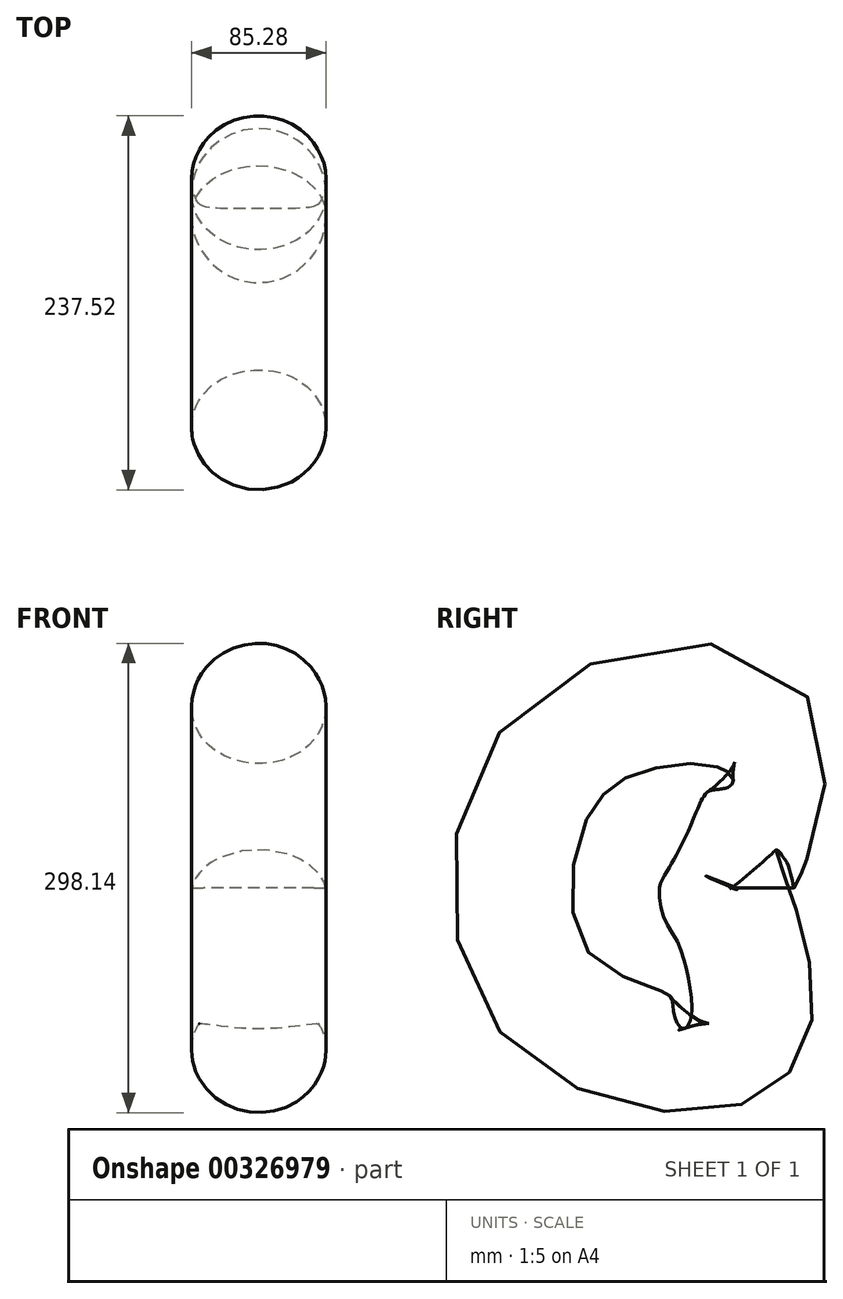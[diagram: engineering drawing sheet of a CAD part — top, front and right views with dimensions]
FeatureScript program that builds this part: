
annotation { "Feature Type Name" : "Feature", "Feature Type Description" : "" }
export const myFeature = defineFeature(function(context is Context, id is Id, definition is map)
    precondition{}
    {
        {
            var Q0;
            Q0=qCreatedBy(makeId("Top.planeOp"),FACE);
            var sketch = newSketch(context, id + "F0", { "sketchPlane" : qUnion([Q0])});
            skCircle(sketch, "E0", {"center": v(0, 0) * mm, "radius": 42.64 * mm});
            skSolve(sketch);
        }
        {
            var Q0;
            Q0=qCreatedBy(makeId("Right.planeOp"),FACE);
            var sketch = newSketch(context, id + "F1", { "sketchPlane" : qUnion([Q0])});
            skFitSpline(sketch, "E1", {"points": [v(0, 0) * mm, v(13.67, 29.8) * mm, v(13.67, 103.44) * mm, v(-98.7, 89.02) * mm, v(-130.58, -31.7) * mm, v(-69.85, -94.7) * mm, v(11.39, -86.36) * mm, v(0, -4.37) * mm, v(0, 0) * mm]});
            skSolve(sketch);
        }
        {
            var Q0;
            Q0 = qSketchRegion(id + "F0", true);
            var Q1;
            Q1 = qConstructionFilter(qBodyType(qCreatedBy(id + "F1" ,EDGE), BodyType.WIRE), ConstructionObject.NO);
            sweep(context, id + "F2", {"profiles" : qUnion([Q0]), "path" : qUnion([Q1])});
        }
    });
